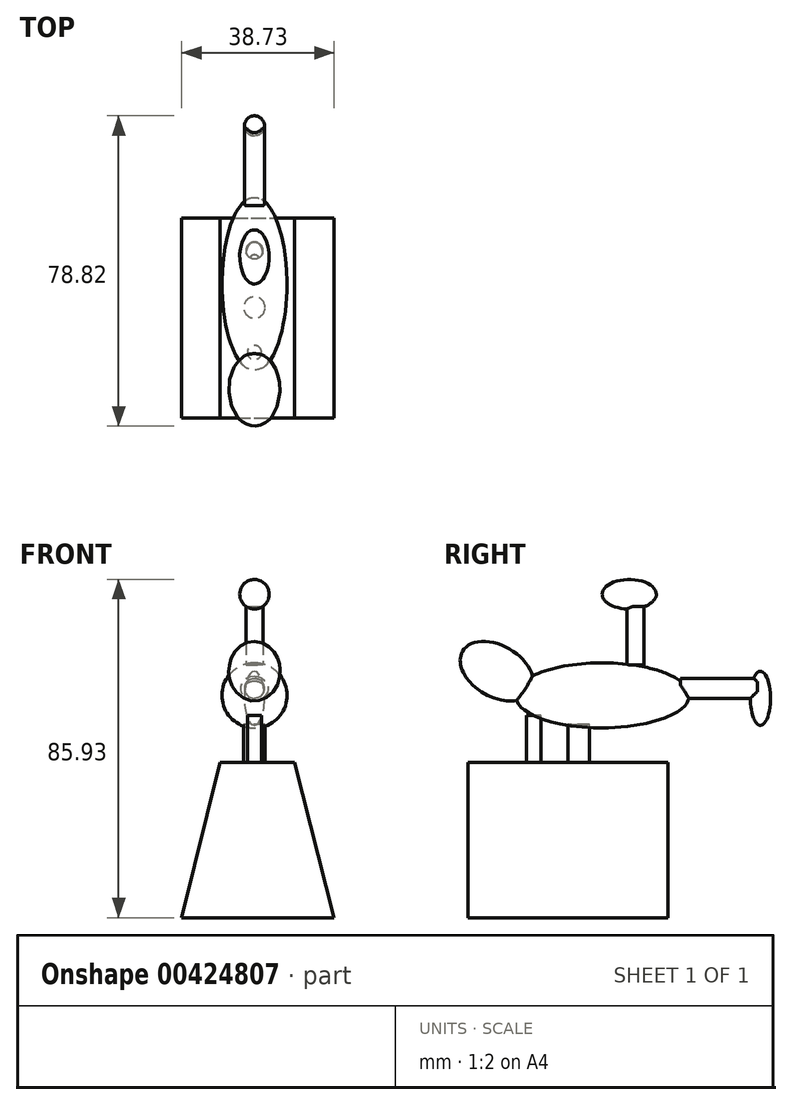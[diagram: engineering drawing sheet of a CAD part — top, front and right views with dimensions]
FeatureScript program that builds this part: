
annotation { "Feature Type Name" : "Feature", "Feature Type Description" : "" }
export const myFeature = defineFeature(function(context is Context, id is Id, definition is map)
    precondition{}
    {
        {
            var Q0;
            Q0=qCreatedBy(makeId("Front.planeOp"),FACE);
            var sketch = newSketch(context, id + "F0", { "sketchPlane" : qUnion([Q0])});
            skLineSegment(sketch, "E0", {"start": v(-18.46, -39.46) * mm, "end": v(-8.69, 0) * mm});
            skLineSegment(sketch, "E1", {"start": v(-8.69, 0) * mm, "end": v(10.14, 0) * mm});
            skLineSegment(sketch, "E2", {"start": v(10.14, 0) * mm, "end": v(20.27, -39.46) * mm});
            skLineSegment(sketch, "E3", {"start": v(-18.46, -39.46) * mm, "end": v(20.27, -39.46) * mm});
            skSolve(sketch);
        }
        {
            var Q0;
            Q0 = qSketchRegion(id + "F0", true);
            extrude(context, id + "F1", {"entities" : qUnion([Q0]), "depth" : 25.4 * mm});
        }
        {
            var Q0;
            Q0 = qSketchRegion(id + "F0", true);
            extrude(context, id + "F2", {"entities" : qUnion([Q0]), "operationType" : NewBodyOperationType.ADD, "oppositeDirection" : true, "depth" : 25.4 * mm});
        }
        {
            var Q0;
            Q0=qCreatedBy(makeId("Right.planeOp"),FACE);
            var sketch = newSketch(context, id + "F3", { "sketchPlane" : qUnion([Q0])});
            skEllipse(sketch, "E4", {"center": v(8.69, 17.02) * mm, "majorRadius": 22.08 * mm, "minorRadius": 8.27 * mm, "majorAxis": v(1, 0)});
            skLineSegment(sketch, "E5", {"start": v(-13.4, 17.02) * mm, "end": v(30.77, 17.02) * mm});
            skSolve(sketch);
        }
        {
            var Q0;
            {var subQ0=sQuery(id+"F3.wireOp",EDGE,"E5");Q0=makeQuery(id+"F3.imprint","IMPRINT",FACE,{"disambiguationData":[TD([[makeQuery(id+"F3.imprint","IMPRINT",EDGE,{"derivedFrom":subQ0}),1.0]])]});}
            var Q1;
            Q1=sQuery(id+"F3.wireOp",EDGE,"E5");
            revolve(context, id + "F4", {"entities" : qUnion([Q0]), "axis" : qUnion([Q1]), "revolveType" : RevolveType.FULL});
        }
        {
            var Q0;
            Q0=qCreatedBy(makeId("Right.planeOp"),FACE);
            var sketch = newSketch(context, id + "F5", { "sketchPlane" : qUnion([Q0])});
            skEllipse(sketch, "E6", {"center": v(-18.1, 23.17) * mm, "majorRadius": 10.06 * mm, "minorRadius": 6.52 * mm, "majorAxis": v(0.86, -0.5)});
            skLineSegment(sketch, "E7", {"start": v(-9.41, 18.1) * mm, "end": v(-26.8, 28.24) * mm});
            skSolve(sketch);
        }
        {
            var Q0;
            {var subQ0=sQuery(id+"F5.wireOp",EDGE,"E7");Q0=makeQuery(id+"F5.imprint","IMPRINT",FACE,{"disambiguationData":[TD([[makeQuery(id+"F5.imprint","IMPRINT",EDGE,{"derivedFrom":subQ0}),-1.0]])]});}
            var Q1;
            Q1=sQuery(id+"F5.wireOp",EDGE,"E7");
            revolve(context, id + "F6", {"operationType" : NewBodyOperationType.ADD, "entities" : qUnion([Q0]), "axis" : qUnion([Q1]), "revolveType" : RevolveType.FULL});
        }
        {
            var Q0;
            Q0=qCreatedBy(makeId("Right.planeOp"),FACE);
            var sketch = newSketch(context, id + "F7", { "sketchPlane" : qUnion([Q0])});
            skLineSegment(sketch, "E8.bottom", {"start": v(-10.5, 11.95) * mm, "end": v(-8.69, 11.95) * mm});
            skLineSegment(sketch, "E8.top", {"start": v(-10.5, 0) * mm, "end": v(-8.69, 0) * mm});
            skLineSegment(sketch, "E8.left", {"start": v(-10.5, 11.95) * mm, "end": v(-10.5, 0) * mm});
            skLineSegment(sketch, "E8.right", {"start": v(-8.69, 11.95) * mm, "end": v(-8.69, 0) * mm});
            skSolve(sketch);
        }
        {
            var Q0;
            Q0 = qSketchRegion(id + "F7", true);
            var Q1;
            Q1=sQuery(id+"F7.wireOp",EDGE,"E8.right");
            revolve(context, id + "F8", {"entities" : qUnion([Q0]), "axis" : qUnion([Q1]), "revolveType" : RevolveType.FULL});
        }
        {
            var Q0;
            Q0=qCreatedBy(makeId("Right.planeOp"),FACE);
            var sketch = newSketch(context, id + "F9", { "sketchPlane" : qUnion([Q0])});
            skLineSegment(sketch, "E9.bottom", {"start": v(28.6, 21.36) * mm, "end": v(48.15, 21.36) * mm});
            skLineSegment(sketch, "E9.top", {"start": v(28.6, 18.83) * mm, "end": v(48.15, 18.83) * mm});
            skLineSegment(sketch, "E9.left", {"start": v(28.6, 21.36) * mm, "end": v(28.6, 18.83) * mm});
            skLineSegment(sketch, "E9.right", {"start": v(48.15, 21.36) * mm, "end": v(48.15, 18.83) * mm});
            skSolve(sketch);
        }
        {
            var Q0;
            Q0 = qSketchRegion(id + "F9", true);
            var Q1;
            Q1=sQuery(id+"F9.wireOp",EDGE,"E9.top");
            revolve(context, id + "F10", {"operationType" : NewBodyOperationType.ADD, "entities" : qUnion([Q0]), "axis" : qUnion([Q1]), "revolveType" : RevolveType.FULL});
        }
        {
            var Q0;
            Q0=qCreatedBy(makeId("Right.planeOp"),FACE);
            var sketch = newSketch(context, id + "F11", { "sketchPlane" : qUnion([Q0])});
            skLineSegment(sketch, "E10.bottom", {"start": v(0, 9.6) * mm, "end": v(2.71, 9.6) * mm});
            skLineSegment(sketch, "E10.top", {"start": v(0, 0) * mm, "end": v(2.71, 0) * mm});
            skLineSegment(sketch, "E10.left", {"start": v(0, 9.6) * mm, "end": v(0, 0) * mm});
            skLineSegment(sketch, "E10.right", {"start": v(2.71, 9.6) * mm, "end": v(2.71, 0) * mm});
            skSolve(sketch);
        }
        {
            var Q0;
            Q0 = qSketchRegion(id + "F11", true);
            var Q1;
            Q1=sQuery(id+"F11.wireOp",EDGE,"E10.right");
            revolve(context, id + "F12", {"entities" : qUnion([Q0]), "axis" : qUnion([Q1]), "revolveType" : RevolveType.FULL});
        }
        {
            var Q0;
            Q0=qCreatedBy(makeId("Right.planeOp"),FACE);
            var sketch = newSketch(context, id + "F13", { "sketchPlane" : qUnion([Q0])});
            skLineSegment(sketch, "E11.bottom", {"start": v(15.02, 24.8) * mm, "end": v(17.19, 24.8) * mm});
            skLineSegment(sketch, "E11.top", {"start": v(15.02, 39.65) * mm, "end": v(17.19, 39.65) * mm});
            skLineSegment(sketch, "E11.left", {"start": v(15.02, 24.8) * mm, "end": v(15.02, 39.65) * mm});
            skLineSegment(sketch, "E11.right", {"start": v(17.19, 24.8) * mm, "end": v(17.19, 39.65) * mm});
            skSolve(sketch);
        }
        {
            var Q0;
            Q0 = qSketchRegion(id + "F13", true);
            var Q1;
            Q1=sQuery(id+"F13.wireOp",EDGE,"E11.right");
            revolve(context, id + "F14", {"operationType" : NewBodyOperationType.ADD, "entities" : qUnion([Q0]), "axis" : qUnion([Q1]), "revolveType" : RevolveType.FULL});
        }
        {
            var Q0;
            Q0=qCreatedBy(makeId("Right.planeOp"),FACE);
            var sketch = newSketch(context, id + "F15", { "sketchPlane" : qUnion([Q0])});
            skEllipse(sketch, "E12", {"center": v(48.87, 16.3) * mm, "majorRadius": 6.88 * mm, "minorRadius": 2.55 * mm, "majorAxis": v(0, 1)});
            skLineSegment(sketch, "E13", {"start": v(48.87, 9.41) * mm, "end": v(48.87, 23.17) * mm});
            skSolve(sketch);
        }
        {
            var Q0;
            {var subQ0=sQuery(id+"F15.wireOp",EDGE,"E13");Q0=makeQuery(id+"F15.imprint","IMPRINT",FACE,{"disambiguationData":[TD([[makeQuery(id+"F15.imprint","IMPRINT",EDGE,{"derivedFrom":subQ0}),-1.0]])]});}
            var Q1;
            Q1=sQuery(id+"F15.wireOp",EDGE,"E13");
            revolve(context, id + "F16", {"operationType" : NewBodyOperationType.ADD, "entities" : qUnion([Q0]), "axis" : qUnion([Q1]), "revolveType" : RevolveType.FULL});
        }
        {
            var Q0;
            Q0=qCreatedBy(makeId("Right.planeOp"),FACE);
            var sketch = newSketch(context, id + "F17", { "sketchPlane" : qUnion([Q0])});
            skEllipse(sketch, "E14", {"center": v(15.57, 42.72) * mm, "majorRadius": 6.88 * mm, "minorRadius": 3.75 * mm, "majorAxis": v(1, 0)});
            skLineSegment(sketch, "E15", {"start": v(8.69, 42.72) * mm, "end": v(22.45, 42.72) * mm});
            skSolve(sketch);
        }
        {
            var Q0;
            {var subQ0=sQuery(id+"F17.wireOp",EDGE,"E15");Q0=makeQuery(id+"F17.imprint","IMPRINT",FACE,{"disambiguationData":[TD([[makeQuery(id+"F17.imprint","IMPRINT",EDGE,{"derivedFrom":subQ0}),1.0]])]});}
            var Q1;
            Q1=sQuery(id+"F17.wireOp",EDGE,"E15");
            revolve(context, id + "F18", {"operationType" : NewBodyOperationType.ADD, "entities" : qUnion([Q0]), "axis" : qUnion([Q1]), "revolveType" : RevolveType.FULL});
        }
    });
